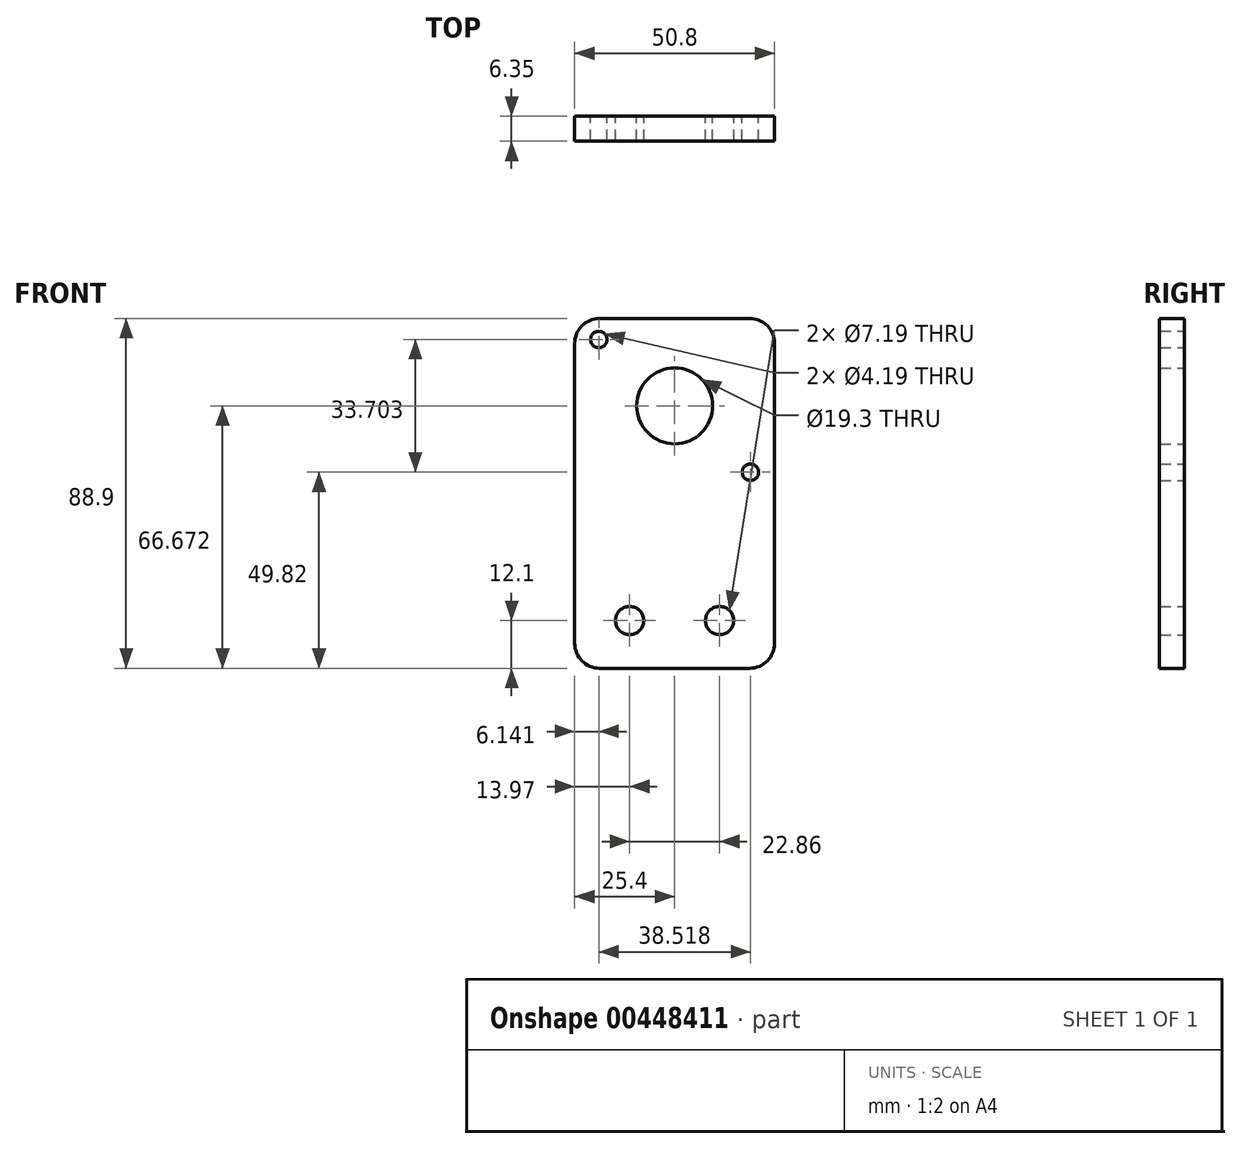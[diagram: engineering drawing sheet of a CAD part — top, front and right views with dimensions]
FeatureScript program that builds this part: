
annotation { "Feature Type Name" : "Feature", "Feature Type Description" : "" }
export const myFeature = defineFeature(function(context is Context, id is Id, definition is map)
    precondition{}
    {
        {
            var Q0;
            Q0=qCreatedBy(makeId("Front.planeOp"),FACE);
            var sketch = newSketch(context, id + "F0", { "sketchPlane" : qUnion([Q0])});
            skPoint(sketch, "E0.middle", {"position": v(0, 0) * mm});
            skCircle(sketch, "E1", {"center": v(0, 54.57) * mm, "radius": 9.65 * mm});
            skPoint(sketch, "E1.centerSnap0", {"position": v(0, 12.7) * mm});
            skLineSegment(sketch, "E2", {"start": v(0, 76.23) * mm, "end": v(0, -39.2) * mm, "construction": true});
            skCircle(sketch, "E3", {"center": v(-11.43, 0) * mm, "radius": 3.6 * mm});
            skCircle(sketch, "E4.MirrorC", {"center": v(11.43, 0) * mm, "radius": 3.6 * mm});
            skPoint(sketch, "E5.visualSharp", {"position": v(-25.4, -12.1) * mm});
            skPoint(sketch, "E6.visualSharp", {"position": v(25.4, -12.1) * mm});
            skCircle(sketch, "E7", {"center": v(19.26, 37.72) * mm, "radius": 2.1 * mm});
            skCircle(sketch, "E8", {"center": v(-19.26, 71.42) * mm, "radius": 2.1 * mm});
            skLineSegment(sketch, "E9.bottom", {"start": v(19.05, -12.1) * mm, "end": v(-19.05, -12.1) * mm});
            skLineSegment(sketch, "E9.top", {"start": v(19.05, 76.8) * mm, "end": v(-19.05, 76.8) * mm});
            skLineSegment(sketch, "E9.left", {"start": v(25.4, -5.75) * mm, "end": v(25.4, 70.45) * mm});
            skLineSegment(sketch, "E9.right", {"start": v(-25.4, -5.75) * mm, "end": v(-25.4, 70.45) * mm});
            skPoint(sketch, "E9.middle", {"position": v(0, 32.35) * mm});
            skLineSegment(sketch, "E10", {"start": v(-33.69, 32.35) * mm, "end": v(43.37, 32.35) * mm, "construction": true});
            skLineSegment(sketch, "E11", {"start": v(-25.4, 76.8) * mm, "end": v(25.4, 32.35) * mm, "construction": true});
            skPoint(sketch, "E12.visualSharp", {"position": v(-25.4, 76.8) * mm});
            skArc(sketch, "E12.filletArc", {"start": v(-19.05, 76.8) * mm, "mid": v(-23.54, 74.94) * mm, "end": v(-25.4, 70.45) * mm});
            skPoint(sketch, "E13.visualSharp", {"position": v(25.4, 76.8) * mm});
            skArc(sketch, "E13.filletArc", {"start": v(25.4, 70.45) * mm, "mid": v(23.54, 74.94) * mm, "end": v(19.05, 76.8) * mm});
            skArc(sketch, "E14.filletArc", {"start": v(19.05, -12.1) * mm, "mid": v(23.54, -10.24) * mm, "end": v(25.4, -5.75) * mm});
            skArc(sketch, "E15.filletArc", {"start": v(-25.4, -5.75) * mm, "mid": v(-23.54, -10.24) * mm, "end": v(-19.05, -12.1) * mm});
            skSolve(sketch);
        }
        {
            var Q0;
            Q0 = qSketchRegion(id + "F0", true);
            extrude(context, id + "F1", {"entities" : qUnion([Q0]), "depth" : 6.35 * mm});
        }
    });
